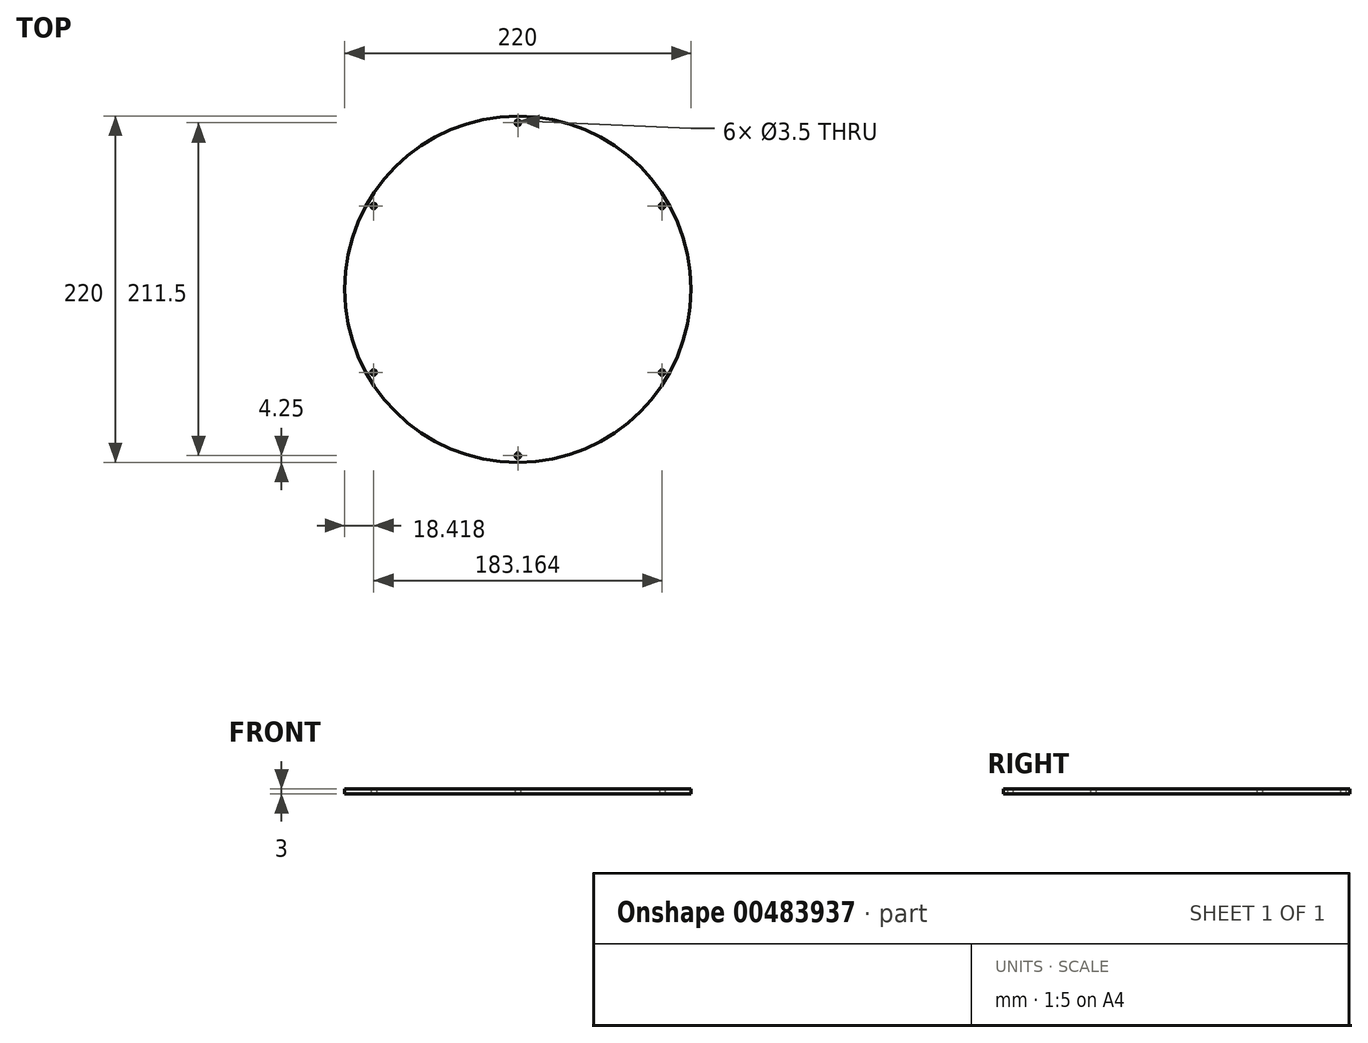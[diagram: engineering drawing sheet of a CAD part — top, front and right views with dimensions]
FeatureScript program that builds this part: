
annotation { "Feature Type Name" : "Feature", "Feature Type Description" : "" }
export const myFeature = defineFeature(function(context is Context, id is Id, definition is map)
    precondition{}
    {
        {
            var Q0;
            Q0=qCreatedBy(makeId("Top.planeOp"),FACE);
            var sketch = newSketch(context, id + "F0", { "sketchPlane" : qUnion([Q0])});
            skCircle(sketch, "E0", {"center": v(0, 0) * mm, "radius": 110 * mm});
            skCircle(sketch, "E1.cCircle", {"center": v(0, 0) * mm, "radius": 105.75 * mm, "construction": true});
            skLineSegment(sketch, "E1.0", {"start": v(0, 105.75) * mm, "end": v(91.58, 52.87) * mm, "construction": true});
            skLineSegment(sketch, "E1.1", {"start": v(91.58, 52.88) * mm, "end": v(91.58, -52.87) * mm, "construction": true});
            skLineSegment(sketch, "E1.2", {"start": v(91.58, -52.87) * mm, "end": v(0, -105.75) * mm, "construction": true});
            skLineSegment(sketch, "E1.3", {"start": v(0, -105.75) * mm, "end": v(-91.58, -52.88) * mm, "construction": true});
            skLineSegment(sketch, "E1.4", {"start": v(-91.58, -52.88) * mm, "end": v(-91.58, 52.88) * mm, "construction": true});
            skLineSegment(sketch, "E1.5", {"start": v(-91.58, 52.88) * mm, "end": v(0, 105.75) * mm, "construction": true});
            skCircle(sketch, "E2", {"center": v(0, 105.75) * mm, "radius": 1.75 * mm});
            skCircle(sketch, "E3.1.0", {"center": v(-91.58, 52.88) * mm, "radius": 1.75 * mm});
            skCircle(sketch, "E3.2.0", {"center": v(-91.58, -52.87) * mm, "radius": 1.75 * mm});
            skCircle(sketch, "E3.3.0", {"center": v(0, -105.75) * mm, "radius": 1.75 * mm});
            skCircle(sketch, "E3.4.0", {"center": v(91.58, -52.88) * mm, "radius": 1.75 * mm});
            skCircle(sketch, "E3.5.0", {"center": v(91.58, 52.88) * mm, "radius": 1.75 * mm});
            skSolve(sketch);
        }
        {
            var Q0;
            Q0=makeQuery(id+"F0.imprint","IMPRINT",FACE,{"disambiguationData":[TD([[makeQuery(id+"F0.imprint","IMPRINT",EDGE,{"derivedFrom":sQuery(id+"F0.wireOp",EDGE,"E0")}),1.0]])]});
            extrude(context, id + "F1", {"entities" : qUnion([Q0]), "depth" : 3 * mm});
        }
    });
